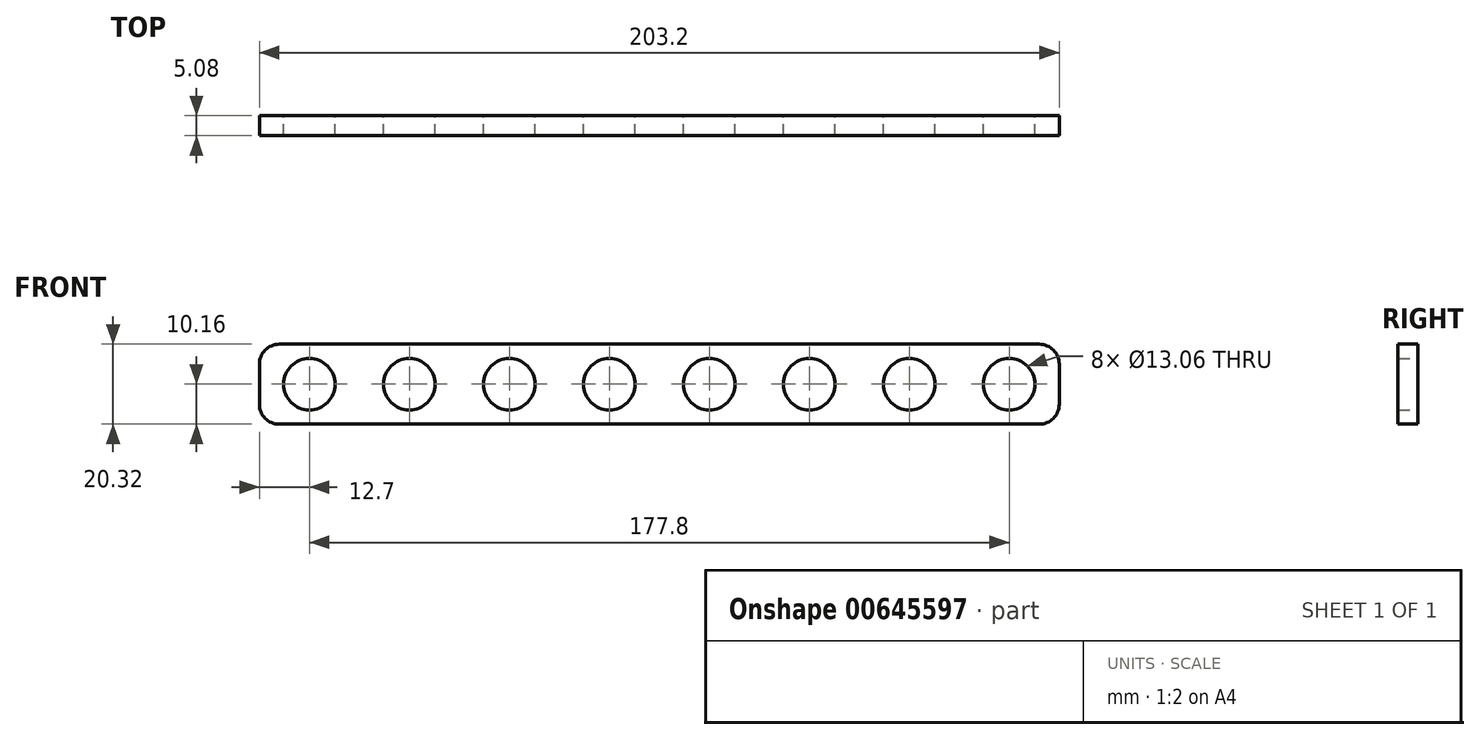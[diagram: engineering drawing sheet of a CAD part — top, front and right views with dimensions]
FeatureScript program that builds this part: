
annotation { "Feature Type Name" : "Feature", "Feature Type Description" : "" }
export const myFeature = defineFeature(function(context is Context, id is Id, definition is map)
    precondition{}
    {
        {
            var Q0;
            Q0=qCreatedBy(makeId("Front.planeOp"),FACE);
            var sketch = newSketch(context, id + "F0", { "sketchPlane" : qUnion([Q0])});
            skLineSegment(sketch, "E0", {"start": v(5.08, 0) * mm, "end": v(198.12, 0) * mm});
            skLineSegment(sketch, "E1", {"start": v(203.2, 5.08) * mm, "end": v(203.2, 15.24) * mm});
            skLineSegment(sketch, "E2", {"start": v(198.12, 20.32) * mm, "end": v(5.08, 20.32) * mm});
            skLineSegment(sketch, "E3", {"start": v(0, 15.24) * mm, "end": v(0, 5.08) * mm});
            skCircle(sketch, "E4", {"center": v(12.7, 10.16) * mm, "radius": 6.53 * mm});
            skPoint(sketch, "E4.centerSnap0", {"position": v(0, 10.16) * mm});
            skPoint(sketch, "E5.endSnap0", {"position": v(101.6, 20.32) * mm});
            skCircle(sketch, "E6.MirrorC", {"center": v(190.5, 10.16) * mm, "radius": 6.53 * mm});
            skPoint(sketch, "E7.visualSharp", {"position": v(0, 20.32) * mm});
            skArc(sketch, "E7.filletArc", {"start": v(5.08, 20.32) * mm, "mid": v(1.49, 18.83) * mm, "end": v(0, 15.24) * mm});
            skPoint(sketch, "E8.visualSharp", {"position": v(0, 0) * mm});
            skArc(sketch, "E8.filletArc", {"start": v(0, 5.08) * mm, "mid": v(1.49, 1.49) * mm, "end": v(5.08, 0) * mm});
            skPoint(sketch, "E9.visualSharp", {"position": v(203.2, 20.32) * mm});
            skArc(sketch, "E9.filletArc", {"start": v(203.2, 15.24) * mm, "mid": v(201.71, 18.83) * mm, "end": v(198.12, 20.32) * mm});
            skPoint(sketch, "E10.visualSharp", {"position": v(203.2, 0) * mm});
            skArc(sketch, "E10.filletArc", {"start": v(198.12, 0) * mm, "mid": v(201.71, 1.49) * mm, "end": v(203.2, 5.08) * mm});
            skCircle(sketch, "E11.1.0.0", {"center": v(38.1, 10.16) * mm, "radius": 6.53 * mm});
            skCircle(sketch, "E11.2.0.0", {"center": v(63.5, 10.16) * mm, "radius": 6.53 * mm});
            skCircle(sketch, "E11.3.0.0", {"center": v(88.9, 10.16) * mm, "radius": 6.53 * mm});
            skCircle(sketch, "E11.4.0.0", {"center": v(114.3, 10.16) * mm, "radius": 6.53 * mm});
            skCircle(sketch, "E11.5.0.0", {"center": v(139.7, 10.16) * mm, "radius": 6.53 * mm});
            skCircle(sketch, "E11.6.0.0", {"center": v(165.1, 10.16) * mm, "radius": 6.53 * mm});
            skLineSegment(sketch, "E11.direction1", {"start": v(12.7, 10.16) * mm, "end": v(38.1, 10.16) * mm, "construction": true});
            skSolve(sketch);
        }
        {
            var Q0;
            Q0=qSketchRegion(id+"F0",true);
            extrude(context, id + "F1", {"entities" : qUnion([Q0]), "depth" : 5.08 * mm, "offsetDistance" : 25.4 * mm});
        }
    });
